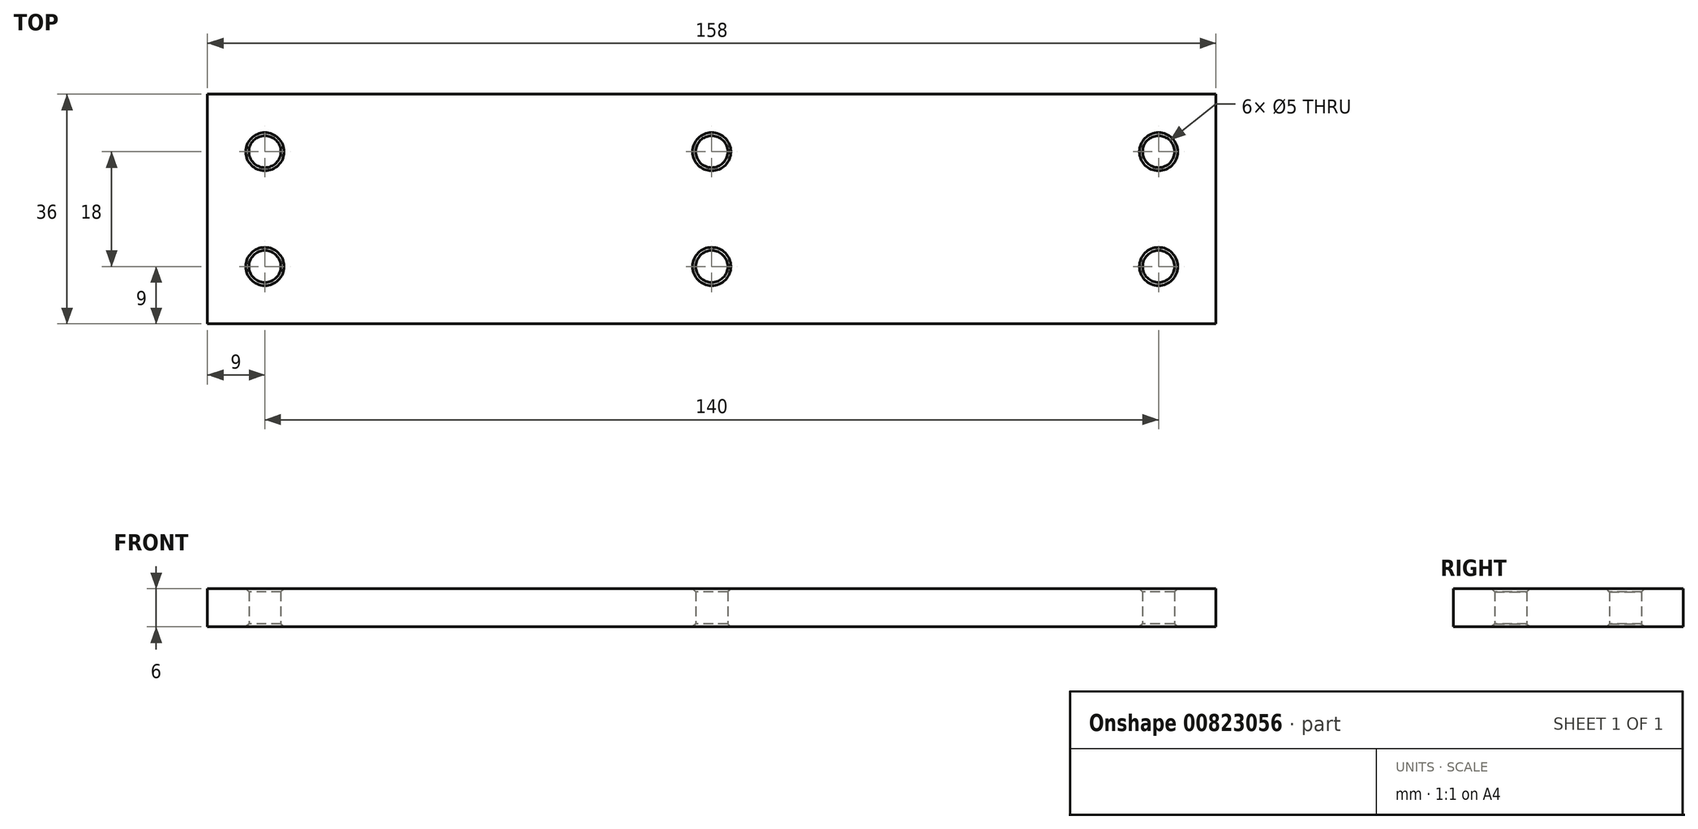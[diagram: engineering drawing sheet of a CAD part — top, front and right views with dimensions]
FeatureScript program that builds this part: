
annotation { "Feature Type Name" : "Feature", "Feature Type Description" : "" }
export const myFeature = defineFeature(function(context is Context, id is Id, definition is map)
    precondition{}
    {
        {
            var Q0;
            Q0=qCreatedBy(makeId("Top.planeOp"),FACE);
            var sketch = newSketch(context, id + "F0", { "sketchPlane" : qUnion([Q0])});
            skLineSegment(sketch, "E0.bottom", {"start": v(-79, -18) * mm, "end": v(79, -18) * mm});
            skLineSegment(sketch, "E0.top", {"start": v(-79, 18) * mm, "end": v(79, 18) * mm});
            skLineSegment(sketch, "E0.left", {"start": v(-79, -18) * mm, "end": v(-79, 18) * mm});
            skLineSegment(sketch, "E0.right", {"start": v(79, -18) * mm, "end": v(79, 18) * mm});
            skPoint(sketch, "E0.middle", {"position": v(0, 0) * mm});
            skLineSegment(sketch, "E1", {"start": v(-79, 0) * mm, "end": v(79, 0) * mm, "construction": true});
            skLineSegment(sketch, "E2", {"start": v(0, 18) * mm, "end": v(0, -18) * mm, "construction": true});
            skLineSegment(sketch, "E3", {"start": v(79, -9) * mm, "end": v(-79, -9) * mm, "construction": true});
            skCircle(sketch, "E4", {"center": v(-70, -9) * mm, "radius": 2.5 * mm});
            skCircle(sketch, "E5", {"center": v(0, -9) * mm, "radius": 2.5 * mm});
            skCircle(sketch, "E6.MirrorC", {"center": v(70, -9) * mm, "radius": 2.5 * mm});
            skCircle(sketch, "E7.MirrorC", {"center": v(70, 9) * mm, "radius": 2.5 * mm});
            skCircle(sketch, "E8.MirrorC", {"center": v(0, 9) * mm, "radius": 2.5 * mm});
            skCircle(sketch, "E9.MirrorC", {"center": v(-70, 9) * mm, "radius": 2.5 * mm});
            skSolve(sketch);
        }
        {
            var Q0;
            Q0 = qSketchRegion(id + "F0", true);
            extrude(context, id + "F1", {"entities" : qUnion([Q0]), "depth" : 6 * mm, "offsetDistance" : 25 * mm});
        }
        {
            var Q0;
            Q0=makeQuery(id+"F1.opExtrude","SWEPT_FACE",FACE,{"disambiguationData":[OSD([sQuery(id+"F0.wireOp",EDGE,"E4")])]});
            var Q1;
            Q1=makeQuery(id+"F1.opExtrude","SWEPT_FACE",FACE,{"disambiguationData":[OSD([sQuery(id+"F0.wireOp",EDGE,"E9.MirrorC")])]});
            var Q2;
            Q2=makeQuery(id+"F1.opExtrude","SWEPT_FACE",FACE,{"disambiguationData":[OSD([sQuery(id+"F0.wireOp",EDGE,"E5")])]});
            var Q3;
            Q3=makeQuery(id+"F1.opExtrude","SWEPT_FACE",FACE,{"disambiguationData":[OSD([sQuery(id+"F0.wireOp",EDGE,"E8.MirrorC")])]});
            var Q4;
            Q4=makeQuery(id+"F1.opExtrude","SWEPT_FACE",FACE,{"disambiguationData":[OSD([sQuery(id+"F0.wireOp",EDGE,"E6.MirrorC")])]});
            var Q5;
            Q5=makeQuery(id+"F1.opExtrude","SWEPT_FACE",FACE,{"disambiguationData":[OSD([sQuery(id+"F0.wireOp",EDGE,"E7.MirrorC")])]});
            chamfer(context, id + "F2", {"entities" : qUnion([Q0, Q1, Q2, Q3, Q4, Q5]), "width" : 0.5 * mm, "tangentPropagation" : true});
        }
    });
